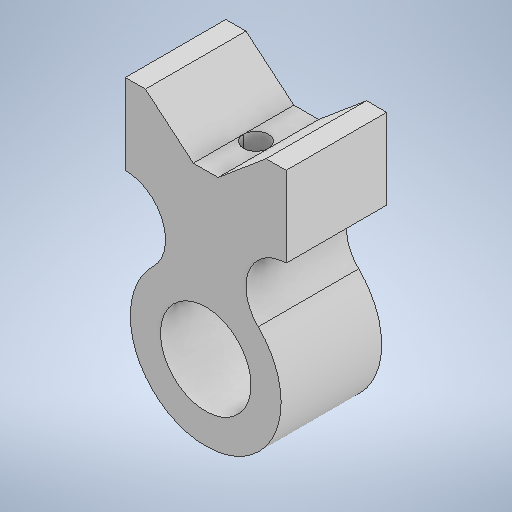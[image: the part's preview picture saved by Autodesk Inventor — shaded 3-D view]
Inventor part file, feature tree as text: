
AUTODESK INVENTOR PART (.ipt)
format: ipt  version: 2025.2 (Build 292293000, 293)  size: 448,512 bytes
history: native  units: in
note: dims shown in document units (in); Inventor stores cm internally (conversion verified against a paired STEP export)
features: extrude x3, sketch x3, other x1
ambient origin geometry x8: Origin, YZ Plane, XZ Plane, XY Plane, X Axis, Y Axis, Z Axis, Center Point
bodies: Solid1 (feature_tree)
feature tree (7):
  extrude  "Extrusion1"  Depth=1.5748in
  extrude  "Extrusion2"  Depth=0.3937in
  extrude  "Extrusion3"  Depth=0.4854in
  sketch  "Sketch1"  dims[d7=3.1496in d8=1.5748in]
  other  "Image1"
  sketch  "Sketch2"  dims[d9=0.3937in d10=0.3937in]
  sketch  "Sketch3"  dims[d16=2.9528in d17=0.7874in d21=1.9685in d22=0.0in d23=1.7717in d24=0.0in d25=0.0in d26=0.4854in d27=0.4854in d28=2.3622in d29=0.0in]
